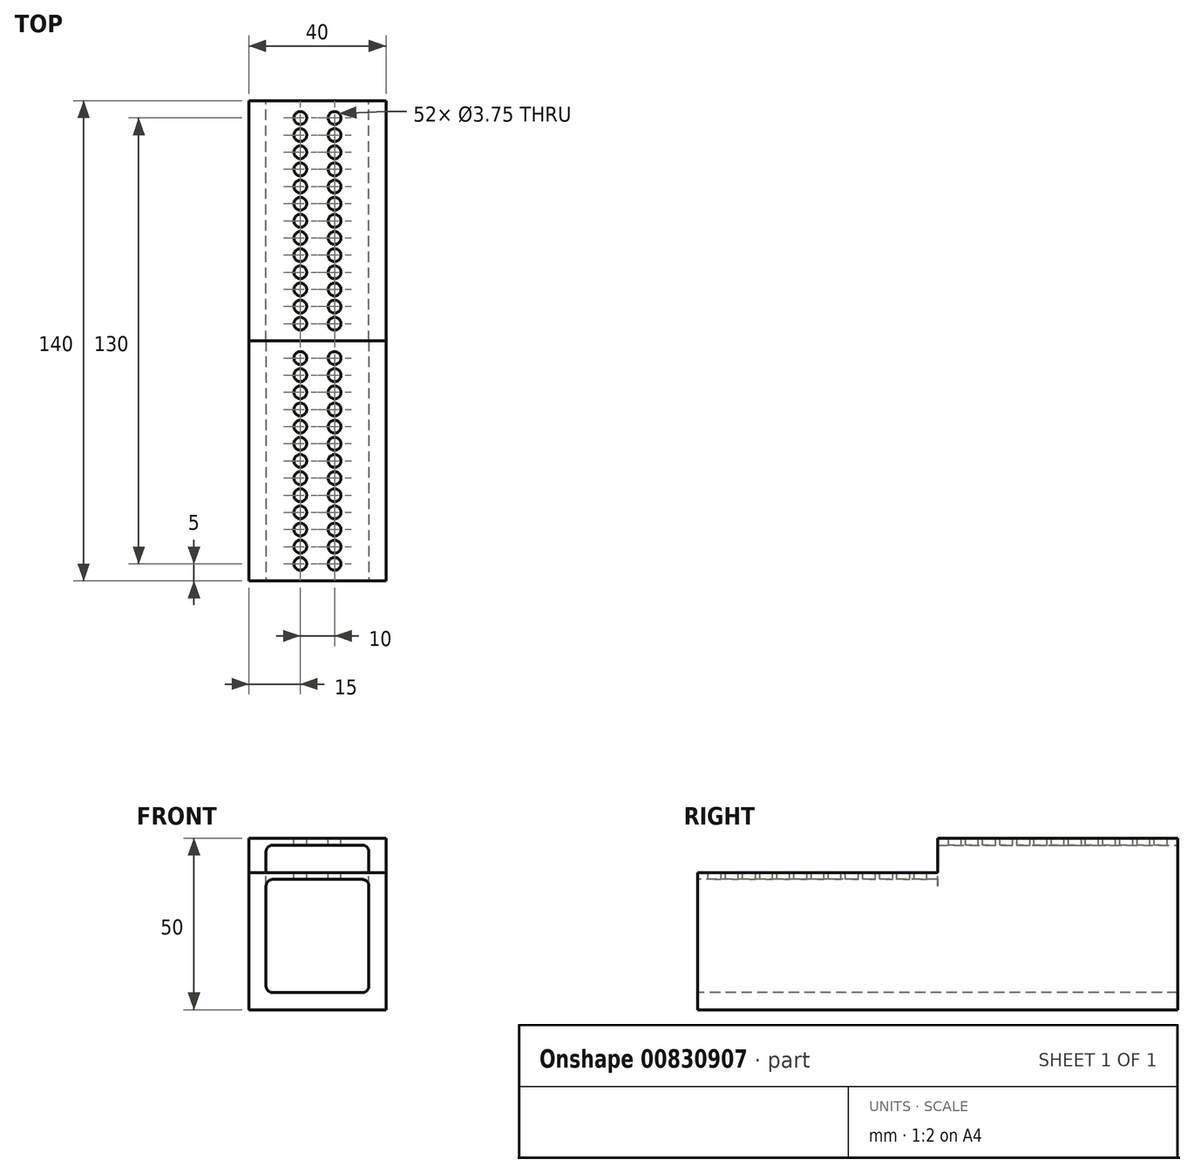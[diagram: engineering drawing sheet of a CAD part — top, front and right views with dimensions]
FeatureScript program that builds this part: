
annotation { "Feature Type Name" : "Feature", "Feature Type Description" : "" }
export const myFeature = defineFeature(function(context is Context, id is Id, definition is map)
    precondition{}
    {
        {
            var Q0;
            Q0=qCreatedBy(makeId("Top.planeOp"),FACE);
            var sketch = newSketch(context, id + "F0", { "sketchPlane" : qUnion([Q0])});
            skLineSegment(sketch, "E0.bottom", {"start": v(-20, 0) * mm, "end": v(20, 0) * mm});
            skLineSegment(sketch, "E0.top", {"start": v(-20, 70) * mm, "end": v(20, 70) * mm});
            skLineSegment(sketch, "E0.left", {"start": v(-20, 0) * mm, "end": v(-20, 70) * mm});
            skLineSegment(sketch, "E0.right", {"start": v(20, 0) * mm, "end": v(20, 70) * mm});
            skSolve(sketch);
        }
        {
            var Q0;
            Q0 = qSketchRegion(id + "F0", true);
            extrude(context, id + "F1", {"entities" : qUnion([Q0]), "depth" : 50 * mm, "offsetDistance" : 25 * mm});
        }
        {
            var Q0;
            Q0=qCreatedBy(makeId("Top.planeOp"),FACE);
            var sketch = newSketch(context, id + "F2", { "sketchPlane" : qUnion([Q0])});
            skLineSegment(sketch, "E1.bottom", {"start": v(-20, 0) * mm, "end": v(20, 0) * mm});
            skLineSegment(sketch, "E1.top", {"start": v(-20, -70) * mm, "end": v(20, -70) * mm});
            skLineSegment(sketch, "E1.left", {"start": v(-20, 0) * mm, "end": v(-20, -70) * mm});
            skLineSegment(sketch, "E1.right", {"start": v(20, 0) * mm, "end": v(20, -70) * mm});
            skSolve(sketch);
        }
        {
            var Q0;
            Q0 = qSketchRegion(id + "F2", true);
            extrude(context, id + "F3", {"entities" : qUnion([Q0]), "operationType" : NewBodyOperationType.ADD, "depth" : 40 * mm, "offsetDistance" : 25 * mm});
        }
        {
            var Q0;
            Q0=makeQuery(id+"F3.opExtrude","SWEPT_FACE",FACE,{"disambiguationData":[OSD([sQuery(id+"F2.wireOp",EDGE,"E1.top")])]});
            var sketch = newSketch(context, id + "F4", { "sketchPlane" : qUnion([Q0])});
            skLineSegment(sketch, "E2.bottom", {"start": v(-15, 5) * mm, "end": v(15, 5) * mm});
            skLineSegment(sketch, "E2.top", {"start": v(-15, 38) * mm, "end": v(15, 38) * mm});
            skLineSegment(sketch, "E2.left", {"start": v(-15, 5) * mm, "end": v(-15, 38) * mm});
            skLineSegment(sketch, "E2.right", {"start": v(15, 5) * mm, "end": v(15, 38) * mm});
            skSolve(sketch);
        }
        {
            var Q0;
            Q0 = qSketchRegion(id + "F4", true);
            extrude(context, id + "F5", {"entities" : qUnion([Q0]), "operationType" : NewBodyOperationType.REMOVE, "oppositeDirection" : true, "depth" : 70 * mm, "offsetDistance" : 25 * mm});
        }
        {
            var Q0;
            Q0=makeQuery(id+"F1.opExtrude","SWEPT_FACE",FACE,{"disambiguationData":[OSD([sQuery(id+"F0.wireOp",EDGE,"E0.top")])]});
            var sketch = newSketch(context, id + "F6", { "sketchPlane" : qUnion([Q0])});
            skLineSegment(sketch, "E3.bottom", {"start": v(-15, 5) * mm, "end": v(15, 5) * mm});
            skLineSegment(sketch, "E3.top", {"start": v(-15, 48) * mm, "end": v(15, 48) * mm});
            skLineSegment(sketch, "E3.left", {"start": v(-15, 5) * mm, "end": v(-15, 48) * mm});
            skLineSegment(sketch, "E3.right", {"start": v(15, 5) * mm, "end": v(15, 48) * mm});
            skSolve(sketch);
        }
        {
            var Q0;
            Q0 = qSketchRegion(id + "F6", true);
            extrude(context, id + "F7", {"entities" : qUnion([Q0]), "operationType" : NewBodyOperationType.REMOVE, "oppositeDirection" : true, "depth" : 70 * mm, "offsetDistance" : 25 * mm});
        }
        {
            var Q0;
            Q0=makeQuery(id+"F7.boolean.opBoolean","MERGE",EDGE,{"derivedFrom":[makeQuery(id+"F5.boolean.opBoolean","COPY",EDGE,{"derivedFrom":makeQuery(id+"F5.opExtrude","SWEPT_EDGE",EDGE,{"disambiguationData":[OSD([sQuery(id+"F4.wireOp",EDGE,"E2.bottom"),sQuery(id+"F4.wireOp",EDGE,"E2.left")])]})}),makeQuery(id+"F7.opExtrude","SWEPT_EDGE",EDGE,{"disambiguationData":[OSD([sQuery(id+"F6.wireOp",EDGE,"E3.bottom"),sQuery(id+"F6.wireOp",EDGE,"E3.right")])]})]});
            var Q1;
            Q1=makeQuery(id+"F7.boolean.opBoolean","MERGE",EDGE,{"derivedFrom":[makeQuery(id+"F5.boolean.opBoolean","COPY",EDGE,{"derivedFrom":makeQuery(id+"F5.opExtrude","SWEPT_EDGE",EDGE,{"disambiguationData":[OSD([sQuery(id+"F4.wireOp",EDGE,"E2.bottom"),sQuery(id+"F4.wireOp",EDGE,"E2.right")])]})}),makeQuery(id+"F7.opExtrude","SWEPT_EDGE",EDGE,{"disambiguationData":[OSD([sQuery(id+"F6.wireOp",EDGE,"E3.bottom"),sQuery(id+"F6.wireOp",EDGE,"E3.left")])]})]});
            var Q2;
            Q2=makeQuery(id+"F5.boolean.opBoolean","COPY",EDGE,{"derivedFrom":makeQuery(id+"F5.opExtrude","SWEPT_EDGE",EDGE,{"disambiguationData":[OSD([sQuery(id+"F4.wireOp",EDGE,"E2.top"),sQuery(id+"F4.wireOp",EDGE,"E2.right")])]})});
            var Q3;
            Q3=makeQuery(id+"F5.boolean.opBoolean","COPY",EDGE,{"derivedFrom":makeQuery(id+"F5.opExtrude","SWEPT_EDGE",EDGE,{"disambiguationData":[OSD([sQuery(id+"F4.wireOp",EDGE,"E2.top"),sQuery(id+"F4.wireOp",EDGE,"E2.left")])]})});
            var Q4;
            Q4=makeQuery(id+"F7.boolean.opBoolean","COPY",EDGE,{"derivedFrom":makeQuery(id+"F7.opExtrude","SWEPT_EDGE",EDGE,{"disambiguationData":[OSD([sQuery(id+"F6.wireOp",EDGE,"E3.top"),sQuery(id+"F6.wireOp",EDGE,"E3.left")])]})});
            var Q5;
            Q5=makeQuery(id+"F7.boolean.opBoolean","COPY",EDGE,{"derivedFrom":makeQuery(id+"F7.opExtrude","SWEPT_EDGE",EDGE,{"disambiguationData":[OSD([sQuery(id+"F6.wireOp",EDGE,"E3.top"),sQuery(id+"F6.wireOp",EDGE,"E3.right")])]})});
            fillet(context, id + "F8", {"entities" : qUnion([Q0, Q1, Q2, Q3, Q4, Q5]), "radius" : 2 * mm, "tangentPropagation" : true, "allowEdgeOverflow" : false});
        }
        {
            var Q0;
            Q0=makeQuery(id+"F1.opExtrude","CAP_FACE",FACE,{"disambiguationData":[OSD([sQuery(id+"F0.wireOp",EDGE,"E0.bottom"),sQuery(id+"F0.wireOp",EDGE,"E0.top"),sQuery(id+"F0.wireOp",EDGE,"E0.left"),sQuery(id+"F0.wireOp",EDGE,"E0.right")])],"isStart":false});
            var sketch = newSketch(context, id + "F9", { "sketchPlane" : qUnion([Q0])});
            skLineSegment(sketch, "E4", {"start": v(0, 70) * mm, "end": v(0, 0) * mm, "construction": true});
            skCircle(sketch, "E5", {"center": v(5, 65) * mm, "radius": 1.88 * mm});
            skCircle(sketch, "E6.0.1.0", {"center": v(5, 60) * mm, "radius": 1.88 * mm});
            skCircle(sketch, "E6.0.2.0", {"center": v(5, 55) * mm, "radius": 1.88 * mm});
            skCircle(sketch, "E6.0.3.0", {"center": v(5, 50) * mm, "radius": 1.88 * mm});
            skCircle(sketch, "E6.0.4.0", {"center": v(5, 45) * mm, "radius": 1.88 * mm});
            skCircle(sketch, "E6.0.5.0", {"center": v(5, 40) * mm, "radius": 1.88 * mm});
            skCircle(sketch, "E6.0.6.0", {"center": v(5, 35) * mm, "radius": 1.88 * mm});
            skCircle(sketch, "E6.0.7.0", {"center": v(5, 30) * mm, "radius": 1.88 * mm});
            skCircle(sketch, "E6.0.8.0", {"center": v(5, 25) * mm, "radius": 1.88 * mm});
            skCircle(sketch, "E6.0.9.0", {"center": v(5, 20) * mm, "radius": 1.88 * mm});
            skCircle(sketch, "E6.0.10.0", {"center": v(5, 15) * mm, "radius": 1.88 * mm});
            skCircle(sketch, "E6.0.11.0", {"center": v(5, 10) * mm, "radius": 1.88 * mm});
            skCircle(sketch, "E6.0.12.0", {"center": v(5, 5) * mm, "radius": 1.88 * mm});
            skCircle(sketch, "E6.0.14.0", {"center": v(5, -5) * mm, "radius": 1.88 * mm});
            skCircle(sketch, "E6.0.15.0", {"center": v(5, -10) * mm, "radius": 1.88 * mm});
            skCircle(sketch, "E6.0.16.0", {"center": v(5, -15) * mm, "radius": 1.88 * mm});
            skCircle(sketch, "E6.0.17.0", {"center": v(5, -20) * mm, "radius": 1.88 * mm});
            skCircle(sketch, "E6.0.18.0", {"center": v(5, -25) * mm, "radius": 1.88 * mm});
            skCircle(sketch, "E6.0.19.0", {"center": v(5, -30) * mm, "radius": 1.88 * mm});
            skCircle(sketch, "E6.0.20.0", {"center": v(5, -35) * mm, "radius": 1.88 * mm});
            skCircle(sketch, "E6.0.21.0", {"center": v(5, -40) * mm, "radius": 1.88 * mm});
            skCircle(sketch, "E6.0.22.0", {"center": v(5, -45) * mm, "radius": 1.88 * mm});
            skCircle(sketch, "E6.0.23.0", {"center": v(5, -50) * mm, "radius": 1.88 * mm});
            skCircle(sketch, "E6.0.24.0", {"center": v(5, -55) * mm, "radius": 1.88 * mm});
            skCircle(sketch, "E6.0.25.0", {"center": v(5, -60) * mm, "radius": 1.88 * mm});
            skCircle(sketch, "E6.0.26.0", {"center": v(5, -65) * mm, "radius": 1.88 * mm});
            skCircle(sketch, "E6.1.0.0", {"center": v(-5, 65) * mm, "radius": 1.88 * mm});
            skCircle(sketch, "E6.1.1.0", {"center": v(-5, 60) * mm, "radius": 1.88 * mm});
            skCircle(sketch, "E6.1.2.0", {"center": v(-5, 55) * mm, "radius": 1.88 * mm});
            skCircle(sketch, "E6.1.3.0", {"center": v(-5, 50) * mm, "radius": 1.88 * mm});
            skCircle(sketch, "E6.1.4.0", {"center": v(-5, 45) * mm, "radius": 1.88 * mm});
            skCircle(sketch, "E6.1.5.0", {"center": v(-5, 40) * mm, "radius": 1.88 * mm});
            skCircle(sketch, "E6.1.6.0", {"center": v(-5, 35) * mm, "radius": 1.88 * mm});
            skCircle(sketch, "E6.1.7.0", {"center": v(-5, 30) * mm, "radius": 1.88 * mm});
            skCircle(sketch, "E6.1.8.0", {"center": v(-5, 25) * mm, "radius": 1.88 * mm});
            skCircle(sketch, "E6.1.9.0", {"center": v(-5, 20) * mm, "radius": 1.88 * mm});
            skCircle(sketch, "E6.1.10.0", {"center": v(-5, 15) * mm, "radius": 1.88 * mm});
            skCircle(sketch, "E6.1.11.0", {"center": v(-5, 10) * mm, "radius": 1.88 * mm});
            skCircle(sketch, "E6.1.12.0", {"center": v(-5, 5) * mm, "radius": 1.88 * mm});
            skCircle(sketch, "E6.1.14.0", {"center": v(-5, -5) * mm, "radius": 1.88 * mm});
            skCircle(sketch, "E6.1.15.0", {"center": v(-5, -10) * mm, "radius": 1.88 * mm});
            skCircle(sketch, "E6.1.16.0", {"center": v(-5, -15) * mm, "radius": 1.88 * mm});
            skCircle(sketch, "E6.1.17.0", {"center": v(-5, -20) * mm, "radius": 1.88 * mm});
            skCircle(sketch, "E6.1.18.0", {"center": v(-5, -25) * mm, "radius": 1.88 * mm});
            skCircle(sketch, "E6.1.19.0", {"center": v(-5, -30) * mm, "radius": 1.88 * mm});
            skCircle(sketch, "E6.1.20.0", {"center": v(-5, -35) * mm, "radius": 1.88 * mm});
            skCircle(sketch, "E6.1.21.0", {"center": v(-5, -40) * mm, "radius": 1.88 * mm});
            skCircle(sketch, "E6.1.22.0", {"center": v(-5, -45) * mm, "radius": 1.88 * mm});
            skCircle(sketch, "E6.1.23.0", {"center": v(-5, -50) * mm, "radius": 1.88 * mm});
            skCircle(sketch, "E6.1.24.0", {"center": v(-5, -55) * mm, "radius": 1.88 * mm});
            skCircle(sketch, "E6.1.25.0", {"center": v(-5, -60) * mm, "radius": 1.88 * mm});
            skCircle(sketch, "E6.1.26.0", {"center": v(-5, -65) * mm, "radius": 1.88 * mm});
            skLineSegment(sketch, "E6.direction1", {"start": v(5, 65) * mm, "end": v(-5, 65) * mm, "construction": true});
            skLineSegment(sketch, "E6.direction2", {"start": v(5, 65) * mm, "end": v(5, 60) * mm, "construction": true});
            skSolve(sketch);
        }
        {
            var Q0;
            Q0 = qSketchRegion(id + "F9", true);
            extrude(context, id + "F10", {"entities" : qUnion([Q0]), "operationType" : NewBodyOperationType.REMOVE, "oppositeDirection" : true, "depth" : 15 * mm, "offsetDistance" : 25 * mm});
        }
    });
